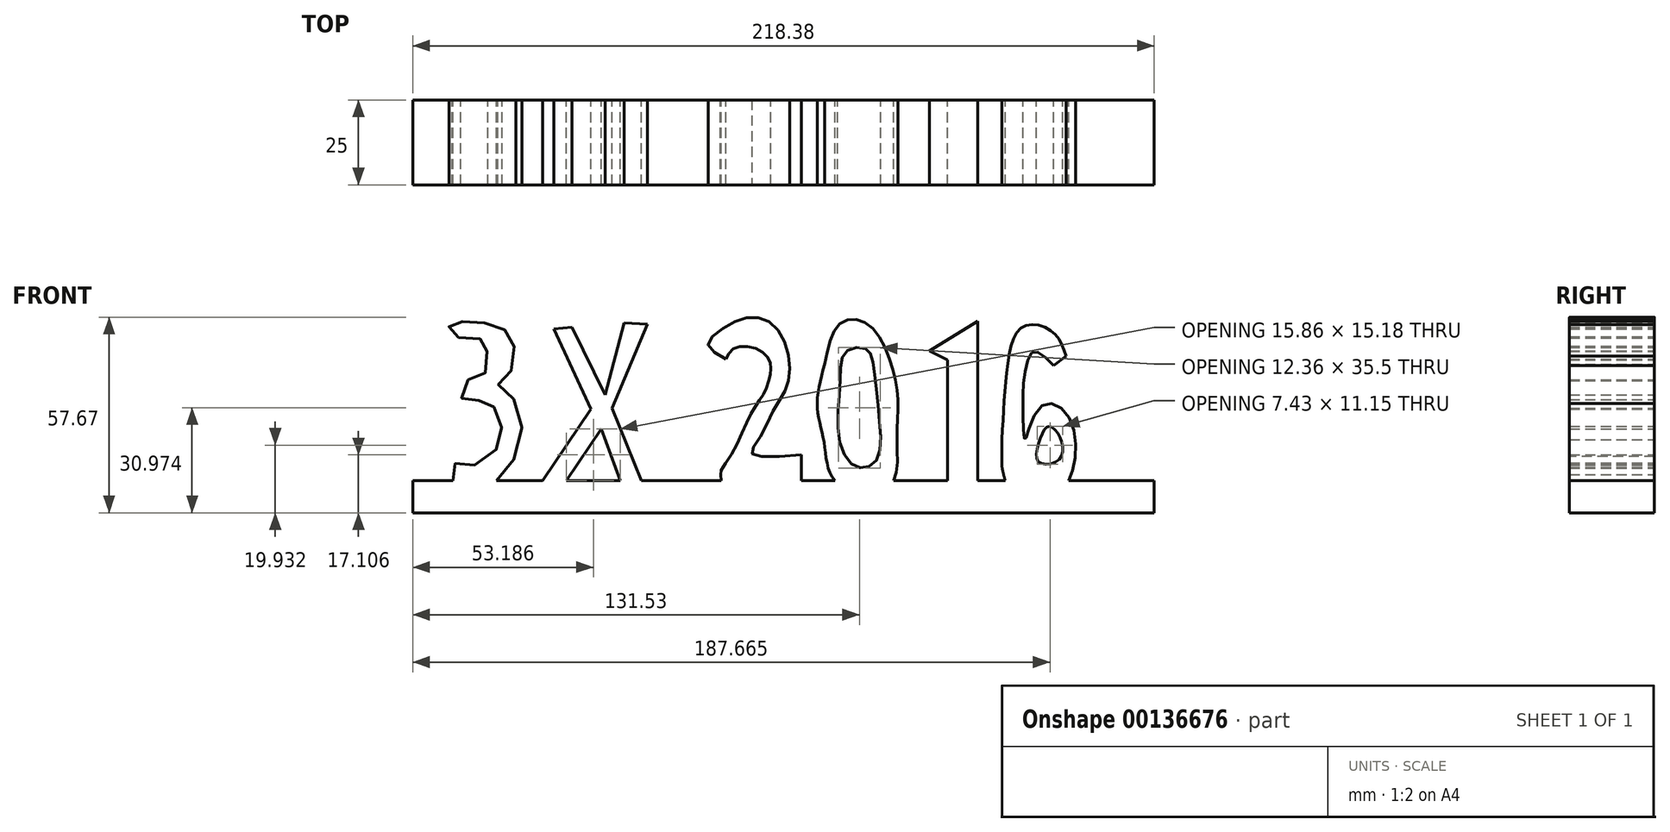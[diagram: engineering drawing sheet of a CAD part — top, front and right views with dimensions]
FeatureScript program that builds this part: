
annotation { "Feature Type Name" : "Feature", "Feature Type Description" : "" }
export const myFeature = defineFeature(function(context is Context, id is Id, definition is map)
    precondition{}
    {
        {
            var Q0;
            Q0=qCreatedBy(makeId("Front.planeOp"),FACE);
            var sketch = newSketch(context, id + "F0", { "sketchPlane" : qUnion([Q0])});
            skFitSpline(sketch, "E0", {"points": [v(-57.92, 34.93) * mm, v(-57.92, 30.5) * mm, v(-54.38, 30.21) * mm, v(-48.78, 29.33) * mm, v(-47.6, 27.26) * mm, v(-47.01, 23.43) * mm, v(-49.66, 17.54) * mm, v(-54.08, 17.24) * mm, v(-54.08, 11.05) * mm, v(-49.37, 11.64) * mm, v(-46.13, 10.76) * mm, v(-43.47, 5.16) * mm, v(-43.18, 0) * mm, v(-49.37, -7.22) * mm, v(-55.56, -6.93) * mm, v(-57.33, -7.81) * mm, v(-57.33, -13.12) * mm, v(-57.03, -15.77) * mm, v(-51.43, -15.18) * mm, v(-45.54, -12.82) * mm, v(-39.64, -6.34) * mm, v(-37.28, 6.93) * mm, v(-42, 14.59) * mm, v(-44.06, 16.65) * mm, v(-39.64, 21.07) * mm, v(-39.64, 28.74) * mm, v(-42, 32.27) * mm, v(-47.6, 34.34) * mm, v(-53.8, 34.63) * mm, v(-57.92, 34.93) * mm]});
            skLineSegment(sketch, "E1", {"start": v(-27.56, 32.57) * mm, "end": v(-16.65, 8.99) * mm});
            skLineSegment(sketch, "E2", {"start": v(-16.65, 8.99) * mm, "end": v(-32.86, -14.88) * mm});
            skLineSegment(sketch, "E3", {"start": v(-32.86, -14.88) * mm, "end": v(-25.79, -14.88) * mm});
            skLineSegment(sketch, "E4", {"start": v(-25.79, -14.88) * mm, "end": v(-13.7, 3.1) * mm});
            skLineSegment(sketch, "E5", {"start": v(-13.7, 3.1) * mm, "end": v(-6.34, -16.65) * mm});
            skLineSegment(sketch, "E6", {"start": v(-6.34, -16.65) * mm, "end": v(0, -16.65) * mm});
            skLineSegment(sketch, "E7", {"start": v(0, -16.65) * mm, "end": v(-10.46, 9.28) * mm});
            skLineSegment(sketch, "E8", {"start": v(-10.46, 9.28) * mm, "end": v(0, 34.04) * mm});
            skLineSegment(sketch, "E9", {"start": v(0, 34.04) * mm, "end": v(-6.93, 34.34) * mm});
            skLineSegment(sketch, "E10", {"start": v(-6.93, 34.34) * mm, "end": v(-12.53, 13.12) * mm});
            skLineSegment(sketch, "E11", {"start": v(-12.53, 13.12) * mm, "end": v(-22.25, 33.16) * mm});
            skLineSegment(sketch, "E12", {"start": v(-22.25, 33.16) * mm, "end": v(-27.56, 32.57) * mm});
            skLineSegment(sketch, "E13", {"start": v(-63.27, -12.08) * mm, "end": v(14.18, -12.08) * mm});
            skLineSegment(sketch, "E14", {"start": v(-63.27, -12.08) * mm, "end": v(-69.16, -12.08) * mm});
            skLineSegment(sketch, "E15", {"start": v(-69.16, -12.08) * mm, "end": v(-69.16, -21.6) * mm});
            skLineSegment(sketch, "E16", {"start": v(-69.16, -21.6) * mm, "end": v(14.18, -21.6) * mm});
            skLineSegment(sketch, "E17", {"start": v(14.18, -21.6) * mm, "end": v(14.18, -12.08) * mm});
            skFitSpline(sketch, "E18", {"points": [v(23.06, 23.7) * mm, v(25.85, 27.1) * mm, v(32.65, 26.48) * mm, v(36.05, 22.77) * mm, v(36.05, 18.75) * mm, v(34.2, 13.5) * mm, v(30.8, 8.24) * mm, v(24.6, -4.44) * mm, v(21.52, -10.32) * mm, v(26.77, -10.62) * mm, v(32.03, -10.32) * mm, v(36.98, -10) * mm], "startDerivative": vector(26.16, 53.37) * mm, "endDerivative": vector(61.05, 4.12) * mm});
            skLineSegment(sketch, "E19", {"start": v(36.98, -10) * mm, "end": v(36.98, -15.57) * mm});
            skFitSpline(sketch, "E20", {"points": [v(23.06, 23.7) * mm, v(17.8, 28.03) * mm, v(23.06, 33.28) * mm, v(31.1, 36.07) * mm, v(37.9, 32.98) * mm, v(41.62, 23.7) * mm, v(41, 15.66) * mm, v(37.6, 9.47) * mm, v(32.65, 0) * mm, v(30.8, -4.13) * mm, v(45.33, -4.44) * mm], "startDerivative": vector(-86.28, 44.8) * mm, "endDerivative": vector(153.75, 13.18) * mm});
            skLineSegment(sketch, "E21", {"start": v(45.33, -4.44) * mm, "end": v(45.33, -14.64) * mm});
            skLineSegment(sketch, "E22", {"start": v(45.33, -14.64) * mm, "end": v(21.83, -14.64) * mm});
            skLineSegment(sketch, "E23", {"start": v(21.83, -14.64) * mm, "end": v(21.52, -10) * mm});
            skFitSpline(sketch, "E24", {"points": [v(66.35, 22.77) * mm, v(64.19, 26.8) * mm, v(58.31, 25.86) * mm, v(56.77, 18.13) * mm, v(56.46, 0) * mm, v(61.72, -8.15) * mm, v(67.28, -6.3) * mm, v(68.2, 6.38) * mm, v(66.35, 22.77) * mm]});
            skFitSpline(sketch, "E25", {"points": [v(52.13, 22.15) * mm, v(56.77, 34.21) * mm, v(64.5, 34.21) * mm, v(71.61, 22.77) * mm, v(73.77, 11.02) * mm, v(73.47, 0) * mm, v(72.54, -11.86) * mm, v(67.28, -15.26) * mm], "startDerivative": vector(18.45, 94.33) * mm, "endDerivative": vector(-57.29, -20) * mm});
            skFitSpline(sketch, "E26", {"points": [v(67.28, -15.26) * mm, v(60.17, -15.26) * mm, v(53.98, -10.32) * mm, v(51.82, 0) * mm, v(49.96, 9.78) * mm, v(52.13, 22.15) * mm], "startDerivative": vector(-41.43, -5.58) * mm, "endDerivative": vector(15.01, 55.95) * mm});
            skLineSegment(sketch, "E27", {"start": v(14.18, -12.08) * mm, "end": v(149.22, -12.08) * mm});
            skLineSegment(sketch, "E28", {"start": v(149.22, -12.08) * mm, "end": v(149.22, -21.6) * mm});
            skLineSegment(sketch, "E29", {"start": v(149.22, -21.6) * mm, "end": v(14.18, -21.6) * mm});
            skLineSegment(sketch, "E30", {"start": v(88.3, 23.39) * mm, "end": v(88.3, -15.57) * mm});
            skLineSegment(sketch, "E31", {"start": v(88.3, -15.57) * mm, "end": v(97.28, -15.88) * mm});
            skLineSegment(sketch, "E32", {"start": v(97.28, -15.88) * mm, "end": v(97.28, 34.83) * mm});
            skLineSegment(sketch, "E33", {"start": v(97.28, 34.83) * mm, "end": v(83.05, 26.17) * mm});
            skLineSegment(sketch, "E34", {"start": v(83.05, 26.17) * mm, "end": v(88.3, 23.39) * mm});
            skFitSpline(sketch, "E35", {"points": [v(123.25, 24.63) * mm, v(119.23, 31.74) * mm, v(110.57, 33.28) * mm, v(105.93, 21.23) * mm, v(104.39, 0) * mm], "startDerivative": vector(-12.93, 38.95) * mm, "endDerivative": vector(-3.15, -65.67) * mm});
            skFitSpline(sketch, "E36", {"points": [v(104.39, 0) * mm, v(104.39, -8.15) * mm], "startDerivative": vector(0, -8.15) * mm, "endDerivative": vector(0, -8.15) * mm});
            skFitSpline(sketch, "E37", {"points": [v(104.39, -8.15) * mm, v(108.1, -15.88) * mm, v(120.16, -15.88) * mm, v(125.41, -8.15) * mm, v(123.87, 6.93) * mm, v(115.83, 9.78) * mm, v(111.2, 0) * mm, v(110.57, 6.93) * mm, v(110.88, 17.82) * mm, v(113.66, 25.86) * mm, v(119.54, 21.84) * mm], "startDerivative": vector(19.3, -97.84) * mm, "endDerivative": vector(76.74, -80.17) * mm});
            skLineSegment(sketch, "E38", {"start": v(119.54, 21.84) * mm, "end": v(123.25, 24.63) * mm});
            skFitSpline(sketch, "E39", {"points": [v(118.3, 3.9) * mm, v(115.52, 0) * mm, v(115.2, -6.6) * mm, v(121.09, -5.99) * mm, v(121.7, 0) * mm, v(118.3, 3.9) * mm]});
            skSolve(sketch);
        }
        {
            var Q0;
            Q0 = qSketchRegion(id + "F0", true);
            extrude(context, id + "F1", {"entities" : qUnion([Q0]), "depth" : 25 * mm});
        }
    });
